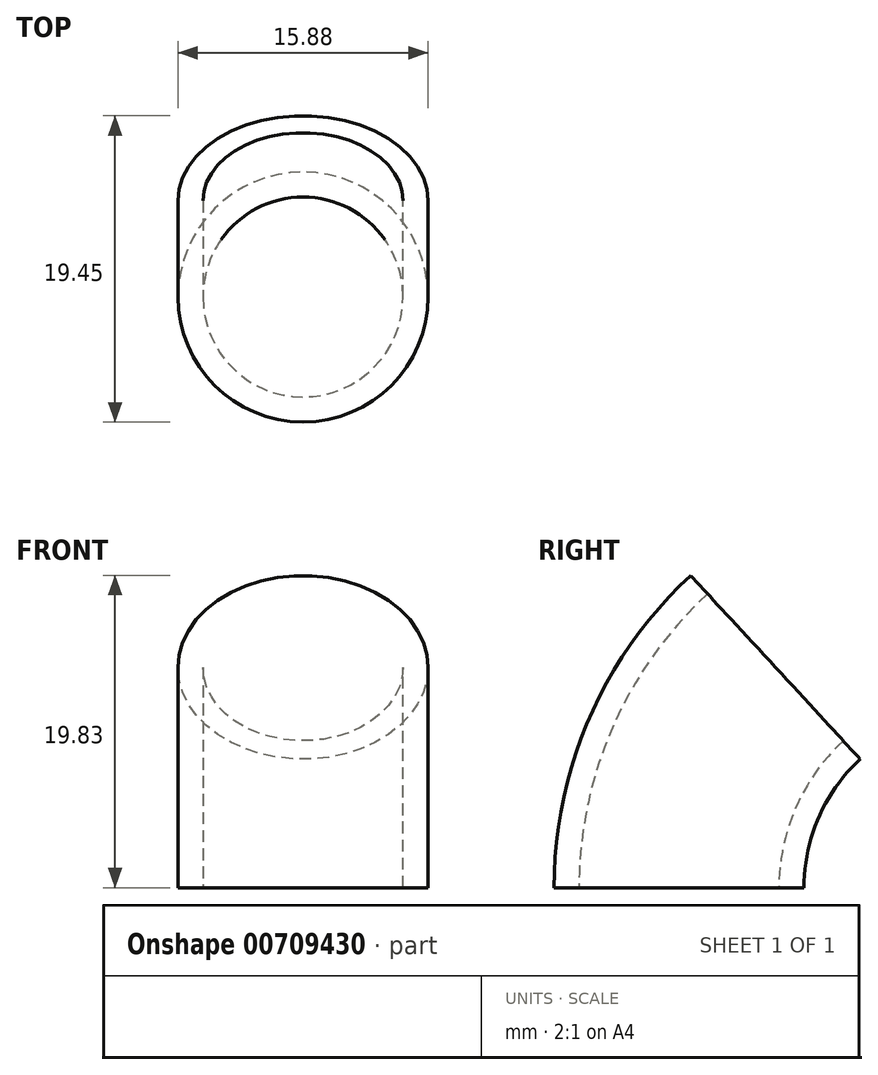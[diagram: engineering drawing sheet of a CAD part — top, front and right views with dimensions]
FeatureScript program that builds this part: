
annotation { "Feature Type Name" : "Feature", "Feature Type Description" : "" }
export const myFeature = defineFeature(function(context is Context, id is Id, definition is map)
    precondition{}
    {
        {
            var Q0;
            Q0=qCreatedBy(makeId("Top.planeOp"),FACE);
            var sketch = newSketch(context, id + "F0", { "sketchPlane" : qUnion([Q0])});
            skLineSegment(sketch, "E0", {"start": v(0, 0) * mm, "end": v(6.35, 0) * mm});
            skCircle(sketch, "E1", {"center": v(0, 0) * mm, "radius": 6.35 * mm});
            skCircle(sketch, "E2.0", {"center": v(0, 0) * mm, "radius": 7.94 * mm});
            skSolve(sketch);
        }
        {
            var Q0;
            Q0=qCreatedBy(makeId("Right.planeOp"),FACE);
            var sketch = newSketch(context, id + "F1", { "sketchPlane" : qUnion([Q0])});
            skLineSegment(sketch, "E3", {"start": v(0, 0) * mm, "end": v(0, 0) * mm});
            skLineSegment(sketch, "E4", {"start": v(0, 0) * mm, "end": v(19.05, 0) * mm});
            skArc(sketch, "E5", {"start": v(0, 0) * mm, "mid": v(1.6, 7.64) * mm, "end": v(6.13, 14) * mm});
            skArc(sketch, "E6", {"start": v(6.13, 14) * mm, "mid": v(12.11, 17.74) * mm, "end": v(19.05, 19.05) * mm});
            skSolve(sketch);
        }
        {
            var Q0;
            Q0=qSketchRegion(id+"F0",true);
            var Q1;
            Q1=sQuery(id+"F1.wireOp",EDGE,"E5");
            sweep(context, id + "F2", {"profiles" : qUnion([Q0]), "path" : qUnion([Q1])});
        }
    });
